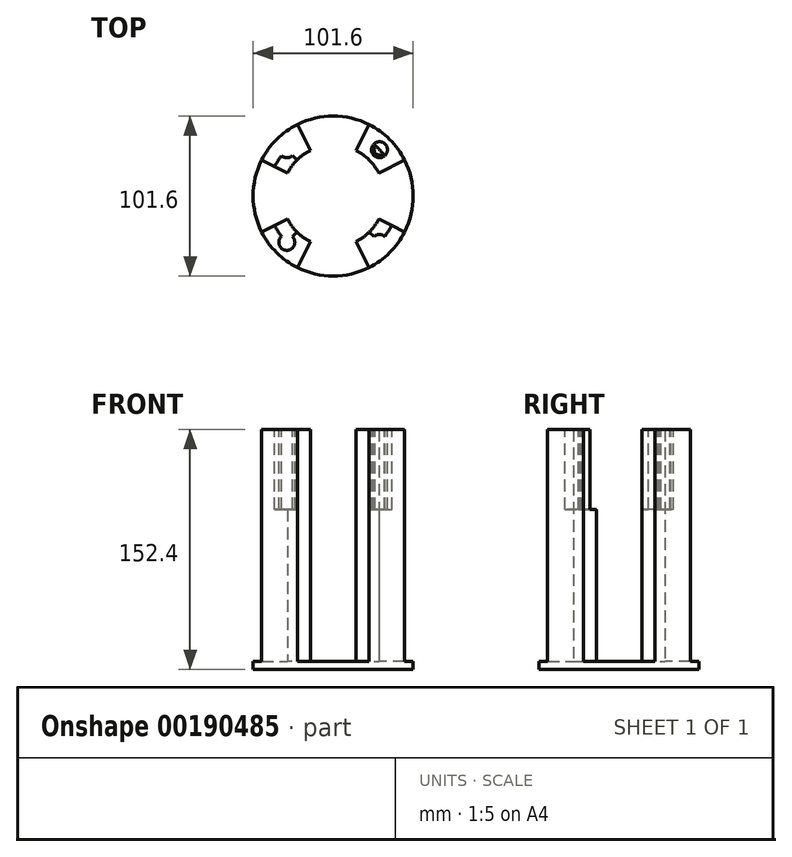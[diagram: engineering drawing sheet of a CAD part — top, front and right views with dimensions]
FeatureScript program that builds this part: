
annotation { "Feature Type Name" : "Feature", "Feature Type Description" : "" }
export const myFeature = defineFeature(function(context is Context, id is Id, definition is map)
    precondition{}
    {
        {
            var Q0;
            Q0=qCreatedBy(makeId("Top.planeOp"),FACE);
            var sketch = newSketch(context, id + "F0", { "sketchPlane" : qUnion([Q0])});
            skLineSegment(sketch, "E0.bottom", {"start": v(0, 0) * mm, "end": v(35.92, 0) * mm});
            skLineSegment(sketch, "E0.top", {"start": v(0, 35.92) * mm, "end": v(35.92, 35.92) * mm});
            skLineSegment(sketch, "E0.left", {"start": v(0, 0) * mm, "end": v(0, 35.92) * mm});
            skLineSegment(sketch, "E0.right", {"start": v(35.92, 0) * mm, "end": v(35.92, 35.92) * mm});
            skCircle(sketch, "E1", {"center": v(0, 0) * mm, "radius": 50.8 * mm});
            skLineSegment(sketch, "E2", {"start": v(0, 0) * mm, "end": v(35.92, 35.92) * mm});
            skPoint(sketch, "E3", {"position": v(17.96, 35.92) * mm});
            skPoint(sketch, "E4", {"position": v(35.92, 17.96) * mm});
            skLineSegment(sketch, "E5", {"start": v(0, 0) * mm, "end": v(17.96, 35.92) * mm});
            skLineSegment(sketch, "E6", {"start": v(0, 0) * mm, "end": v(35.92, 17.96) * mm});
            skLineSegment(sketch, "E7", {"start": v(35.92, 17.96) * mm, "end": v(45.44, 22.72) * mm});
            skLineSegment(sketch, "E8", {"start": v(17.96, 35.92) * mm, "end": v(22.72, 45.44) * mm});
            skCircle(sketch, "E9", {"center": v(0, 0) * mm, "radius": 40.16 * mm});
            skPoint(sketch, "E10.MirrorP", {"position": v(-17.96, 35.92) * mm});
            skPoint(sketch, "E11.MirrorP", {"position": v(-35.92, 17.96) * mm});
            skPoint(sketch, "E12.MirrorP", {"position": v(17.96, -35.92) * mm});
            skPoint(sketch, "E13.MirrorP", {"position": v(35.92, -17.96) * mm});
            skPoint(sketch, "E14.MirrorP", {"position": v(-17.96, -35.92) * mm});
            skPoint(sketch, "E15.MirrorP", {"position": v(-35.92, -17.96) * mm});
            skCircle(sketch, "E16", {"center": v(0, 0) * mm, "radius": 32.43 * mm});
            skLineSegment(sketch, "E17.MirrorCS", {"start": v(0, 0) * mm, "end": v(-17.96, 35.92) * mm});
            skLineSegment(sketch, "E18.MirrorCS", {"start": v(0, 0) * mm, "end": v(-35.92, 17.96) * mm});
            skLineSegment(sketch, "E19.MirrorCS", {"start": v(-35.92, 17.96) * mm, "end": v(-45.44, 22.72) * mm});
            skLineSegment(sketch, "E20.MirrorCS", {"start": v(-17.96, 35.92) * mm, "end": v(-22.72, 45.44) * mm});
            skLineSegment(sketch, "E21.MirrorCS", {"start": v(0, 0) * mm, "end": v(-35.92, -17.96) * mm});
            skLineSegment(sketch, "E22.MirrorCS", {"start": v(0, 0) * mm, "end": v(-17.96, -35.92) * mm});
            skLineSegment(sketch, "E23.MirrorCS", {"start": v(-17.96, -35.92) * mm, "end": v(-22.72, -45.44) * mm});
            skLineSegment(sketch, "E24.MirrorCS", {"start": v(-35.92, -17.96) * mm, "end": v(-45.44, -22.72) * mm});
            skLineSegment(sketch, "E25.MirrorCS", {"start": v(0, 0) * mm, "end": v(17.96, -35.92) * mm});
            skLineSegment(sketch, "E26.MirrorCS", {"start": v(0, 0) * mm, "end": v(35.92, -17.96) * mm});
            skLineSegment(sketch, "E27.MirrorCS", {"start": v(35.92, -17.96) * mm, "end": v(45.44, -22.72) * mm});
            skLineSegment(sketch, "E28.MirrorCS", {"start": v(17.96, -35.92) * mm, "end": v(22.72, -45.44) * mm});
            skSolve(sketch);
        }
        {
            var Q0;
            {var subQ0=sQuery(id+"F0.wireOp",EDGE,"E17.MirrorCS");var subQ1=sQuery(id+"F0.wireOp",EDGE,"E16");var subQ2=makeQuery(id+"F0.imprint","INTERSECT",VERTEX,{"derivedFrom":[subQ1,subQ0]});Q0=makeQuery(id+"F0.imprint","IMPRINT",FACE,{"disambiguationData":[TD([[makeQuery(id+"F0.imprint","IMPRINT",EDGE,{"disambiguationData":[TD([[subQ2,-1.0]])],"derivedFrom":subQ1}),1.0]])]});}
            var Q1;
            {var subQ1=sQuery(id+"F0.wireOp",EDGE,"E0.left");var subQ3=sQuery(id+"F0.wireOp",EDGE,"E16");var subQ4=makeQuery(id+"F0.imprint","INTERSECT",VERTEX,{"derivedFrom":[subQ1,subQ3]});Q1=makeQuery(id+"F0.imprint","IMPRINT",FACE,{"disambiguationData":[TD([[makeQuery(id+"F0.imprint","IMPRINT",EDGE,{"disambiguationData":[TD([[subQ4,-1.0]])],"derivedFrom":subQ3}),1.0]])]});}
            var Q2;
            {var subQ1=sQuery(id+"F0.wireOp",EDGE,"E0.left");var subQ3=sQuery(id+"F0.wireOp",EDGE,"E16");var subQ4=makeQuery(id+"F0.imprint","INTERSECT",VERTEX,{"derivedFrom":[subQ1,subQ3]});Q2=makeQuery(id+"F0.imprint","IMPRINT",FACE,{"disambiguationData":[TD([[makeQuery(id+"F0.imprint","IMPRINT",EDGE,{"disambiguationData":[TD([[subQ4,1.0]])],"derivedFrom":subQ3}),1.0]])]});}
            var Q3;
            {var subQ1=sQuery(id+"F0.wireOp",EDGE,"E2");var subQ3=sQuery(id+"F0.wireOp",EDGE,"E16");var subQ4=makeQuery(id+"F0.imprint","INTERSECT",VERTEX,{"derivedFrom":[subQ1,subQ3]});Q3=makeQuery(id+"F0.imprint","IMPRINT",FACE,{"disambiguationData":[TD([[makeQuery(id+"F0.imprint","IMPRINT",EDGE,{"disambiguationData":[TD([[subQ4,-1.0]])],"derivedFrom":subQ3}),1.0]])]});}
            var Q4;
            {var subQ1=sQuery(id+"F0.wireOp",EDGE,"E2");var subQ3=sQuery(id+"F0.wireOp",EDGE,"E16");var subQ4=makeQuery(id+"F0.imprint","INTERSECT",VERTEX,{"derivedFrom":[subQ1,subQ3]});Q4=makeQuery(id+"F0.imprint","IMPRINT",FACE,{"disambiguationData":[TD([[makeQuery(id+"F0.imprint","IMPRINT",EDGE,{"disambiguationData":[TD([[subQ4,1.0]])],"derivedFrom":subQ3}),1.0]])]});}
            var Q5;
            {var subQ1=sQuery(id+"F0.wireOp",EDGE,"E0.bottom");var subQ3=sQuery(id+"F0.wireOp",EDGE,"E16");var subQ4=makeQuery(id+"F0.imprint","INTERSECT",VERTEX,{"derivedFrom":[subQ1,subQ3]});Q5=makeQuery(id+"F0.imprint","IMPRINT",FACE,{"disambiguationData":[TD([[makeQuery(id+"F0.imprint","IMPRINT",EDGE,{"disambiguationData":[TD([[subQ4,-1.0]])],"derivedFrom":subQ3}),1.0]])]});}
            var Q6;
            {var subQ1=sQuery(id+"F0.wireOp",EDGE,"E0.bottom");var subQ3=sQuery(id+"F0.wireOp",EDGE,"E16");var subQ4=makeQuery(id+"F0.imprint","INTERSECT",VERTEX,{"derivedFrom":[subQ1,subQ3]});Q6=makeQuery(id+"F0.imprint","IMPRINT",FACE,{"disambiguationData":[TD([[makeQuery(id+"F0.imprint","IMPRINT",EDGE,{"disambiguationData":[TD([[subQ4,1.0]])],"derivedFrom":subQ3}),1.0]])]});}
            var Q7;
            {var subQ0=sQuery(id+"F0.wireOp",EDGE,"E25.MirrorCS");var subQ1=sQuery(id+"F0.wireOp",EDGE,"E16");var subQ2=makeQuery(id+"F0.imprint","INTERSECT",VERTEX,{"derivedFrom":[subQ1,subQ0]});Q7=makeQuery(id+"F0.imprint","IMPRINT",FACE,{"disambiguationData":[TD([[makeQuery(id+"F0.imprint","IMPRINT",EDGE,{"disambiguationData":[TD([[subQ2,-1.0]])],"derivedFrom":subQ1}),1.0]])]});}
            var Q8;
            {var subQ0=sQuery(id+"F0.wireOp",EDGE,"E22.MirrorCS");var subQ1=sQuery(id+"F0.wireOp",EDGE,"E16");var subQ2=makeQuery(id+"F0.imprint","INTERSECT",VERTEX,{"derivedFrom":[subQ1,subQ0]});Q8=makeQuery(id+"F0.imprint","IMPRINT",FACE,{"disambiguationData":[TD([[makeQuery(id+"F0.imprint","IMPRINT",EDGE,{"disambiguationData":[TD([[subQ2,-1.0]])],"derivedFrom":subQ1}),1.0]])]});}
            var Q9;
            {var subQ0=sQuery(id+"F0.wireOp",EDGE,"E21.MirrorCS");var subQ1=sQuery(id+"F0.wireOp",EDGE,"E16");var subQ2=makeQuery(id+"F0.imprint","INTERSECT",VERTEX,{"derivedFrom":[subQ1,subQ0]});Q9=makeQuery(id+"F0.imprint","IMPRINT",FACE,{"disambiguationData":[TD([[makeQuery(id+"F0.imprint","IMPRINT",EDGE,{"disambiguationData":[TD([[subQ2,-1.0]])],"derivedFrom":subQ1}),1.0]])]});}
            var Q10;
            {var subQ0=sQuery(id+"F0.wireOp",EDGE,"E18.MirrorCS");var subQ1=sQuery(id+"F0.wireOp",EDGE,"E16");var subQ2=makeQuery(id+"F0.imprint","INTERSECT",VERTEX,{"derivedFrom":[subQ1,subQ0]});Q10=makeQuery(id+"F0.imprint","IMPRINT",FACE,{"disambiguationData":[TD([[makeQuery(id+"F0.imprint","IMPRINT",EDGE,{"disambiguationData":[TD([[subQ2,-1.0]])],"derivedFrom":subQ1}),1.0]])]});}
            var Q11;
            {var subQ0=sQuery(id+"F0.wireOp",EDGE,"E18.MirrorCS");var subQ5=sQuery(id+"F0.wireOp",EDGE,"E16");var subQ6=makeQuery(id+"F0.imprint","INTERSECT",VERTEX,{"derivedFrom":[subQ5,subQ0]});Q11=makeQuery(id+"F0.imprint","IMPRINT",FACE,{"disambiguationData":[TD([[makeQuery(id+"F0.imprint","IMPRINT",EDGE,{"disambiguationData":[TD([[subQ6,-1.0]])],"derivedFrom":subQ5}),-1.0]])]});}
            var Q12;
            {var subQ0=sQuery(id+"F0.wireOp",EDGE,"E17.MirrorCS");var subQ5=sQuery(id+"F0.wireOp",EDGE,"E16");var subQ6=makeQuery(id+"F0.imprint","INTERSECT",VERTEX,{"derivedFrom":[subQ5,subQ0]});Q12=makeQuery(id+"F0.imprint","IMPRINT",FACE,{"disambiguationData":[TD([[makeQuery(id+"F0.imprint","IMPRINT",EDGE,{"disambiguationData":[TD([[subQ6,-1.0]])],"derivedFrom":subQ5}),-1.0]])]});}
            var Q13;
            {var subQ1=sQuery(id+"F0.wireOp",EDGE,"E0.top");var subQ5=sQuery(id+"F0.wireOp",EDGE,"E0.left");var subQ6=makeQuery(id+"F0.imprint","INTERSECT",VERTEX,{"derivedFrom":[subQ1,subQ5]});Q13=makeQuery(id+"F0.imprint","IMPRINT",FACE,{"disambiguationData":[TD([[makeQuery(id+"F0.imprint","IMPRINT",EDGE,{"disambiguationData":[TD([[subQ6,1.0]])],"derivedFrom":subQ5}),1.0]])]});}
            var Q14;
            {var subQ0=sQuery(id+"F0.wireOp",EDGE,"E0.left");var subQ1=sQuery(id+"F0.wireOp",EDGE,"E0.top");var subQ2=makeQuery(id+"F0.imprint","INTERSECT",VERTEX,{"derivedFrom":[subQ1,subQ0]});Q14=makeQuery(id+"F0.imprint","IMPRINT",FACE,{"disambiguationData":[TD([[makeQuery(id+"F0.imprint","IMPRINT",EDGE,{"disambiguationData":[TD([[subQ2,1.0]])],"derivedFrom":subQ0}),-1.0]])]});}
            var Q15;
            {var subQ0=sQuery(id+"F0.wireOp",EDGE,"E16");var subQ1=sQuery(id+"F0.wireOp",EDGE,"E2");var subQ2=makeQuery(id+"F0.imprint","INTERSECT",VERTEX,{"derivedFrom":[subQ1,subQ0]});Q15=makeQuery(id+"F0.imprint","IMPRINT",FACE,{"disambiguationData":[TD([[makeQuery(id+"F0.imprint","IMPRINT",EDGE,{"disambiguationData":[TD([[subQ2,-1.0]])],"derivedFrom":subQ1}),1.0]])]});}
            var Q16;
            {var subQ0=sQuery(id+"F0.wireOp",EDGE,"E2");var subQ3=sQuery(id+"F0.wireOp",EDGE,"E9");var subQ5=makeQuery(id+"F0.imprint","INTERSECT",VERTEX,{"derivedFrom":[subQ0,subQ3]});Q16=makeQuery(id+"F0.imprint","IMPRINT",FACE,{"disambiguationData":[TD([[makeQuery(id+"F0.imprint","IMPRINT",EDGE,{"disambiguationData":[TD([[subQ5,-1.0]])],"derivedFrom":subQ0}),1.0]])]});}
            var Q17;
            {var subQ0=sQuery(id+"F0.wireOp",EDGE,"E2");var subQ3=sQuery(id+"F0.wireOp",EDGE,"E9");var subQ5=makeQuery(id+"F0.imprint","INTERSECT",VERTEX,{"derivedFrom":[subQ0,subQ3]});Q17=makeQuery(id+"F0.imprint","IMPRINT",FACE,{"disambiguationData":[TD([[makeQuery(id+"F0.imprint","IMPRINT",EDGE,{"disambiguationData":[TD([[subQ5,-1.0]])],"derivedFrom":subQ0}),-1.0]])]});}
            var Q18;
            {var subQ0=sQuery(id+"F0.wireOp",EDGE,"E16");var subQ1=sQuery(id+"F0.wireOp",EDGE,"E2");var subQ2=makeQuery(id+"F0.imprint","INTERSECT",VERTEX,{"derivedFrom":[subQ1,subQ0]});Q18=makeQuery(id+"F0.imprint","IMPRINT",FACE,{"disambiguationData":[TD([[makeQuery(id+"F0.imprint","IMPRINT",EDGE,{"disambiguationData":[TD([[subQ2,-1.0]])],"derivedFrom":subQ1}),-1.0]])]});}
            var Q19;
            {var subQ0=sQuery(id+"F0.wireOp",EDGE,"E0.right");var subQ1=sQuery(id+"F0.wireOp",EDGE,"E0.bottom");var subQ2=makeQuery(id+"F0.imprint","INTERSECT",VERTEX,{"derivedFrom":[subQ1,subQ0]});Q19=makeQuery(id+"F0.imprint","IMPRINT",FACE,{"disambiguationData":[TD([[makeQuery(id+"F0.imprint","IMPRINT",EDGE,{"disambiguationData":[TD([[subQ2,1.0]])],"derivedFrom":subQ1}),1.0]])]});}
            var Q20;
            {var subQ1=sQuery(id+"F0.wireOp",EDGE,"E0.bottom");var subQ6=sQuery(id+"F0.wireOp",EDGE,"E0.right");var subQ9=makeQuery(id+"F0.imprint","INTERSECT",VERTEX,{"derivedFrom":[subQ1,subQ6]});Q20=makeQuery(id+"F0.imprint","IMPRINT",FACE,{"disambiguationData":[TD([[makeQuery(id+"F0.imprint","IMPRINT",EDGE,{"disambiguationData":[TD([[subQ9,1.0]])],"derivedFrom":subQ1}),-1.0]])]});}
            var Q21;
            {var subQ0=sQuery(id+"F0.wireOp",EDGE,"E25.MirrorCS");var subQ5=sQuery(id+"F0.wireOp",EDGE,"E16");var subQ6=makeQuery(id+"F0.imprint","INTERSECT",VERTEX,{"derivedFrom":[subQ5,subQ0]});Q21=makeQuery(id+"F0.imprint","IMPRINT",FACE,{"disambiguationData":[TD([[makeQuery(id+"F0.imprint","IMPRINT",EDGE,{"disambiguationData":[TD([[subQ6,-1.0]])],"derivedFrom":subQ5}),-1.0]])]});}
            var Q22;
            {var subQ0=sQuery(id+"F0.wireOp",EDGE,"E22.MirrorCS");var subQ5=sQuery(id+"F0.wireOp",EDGE,"E16");var subQ6=makeQuery(id+"F0.imprint","INTERSECT",VERTEX,{"derivedFrom":[subQ5,subQ0]});Q22=makeQuery(id+"F0.imprint","IMPRINT",FACE,{"disambiguationData":[TD([[makeQuery(id+"F0.imprint","IMPRINT",EDGE,{"disambiguationData":[TD([[subQ6,-1.0]])],"derivedFrom":subQ5}),-1.0]])]});}
            var Q23;
            {var subQ0=sQuery(id+"F0.wireOp",EDGE,"E21.MirrorCS");var subQ5=sQuery(id+"F0.wireOp",EDGE,"E16");var subQ6=makeQuery(id+"F0.imprint","INTERSECT",VERTEX,{"derivedFrom":[subQ5,subQ0]});Q23=makeQuery(id+"F0.imprint","IMPRINT",FACE,{"disambiguationData":[TD([[makeQuery(id+"F0.imprint","IMPRINT",EDGE,{"disambiguationData":[TD([[subQ6,-1.0]])],"derivedFrom":subQ5}),-1.0]])]});}
            var Q24;
            {var subQ0=sQuery(id+"F0.wireOp",EDGE,"E23.MirrorCS");Q24=makeQuery(id+"F0.imprint","IMPRINT",FACE,{"disambiguationData":[TD([[makeQuery(id+"F0.imprint","IMPRINT",EDGE,{"derivedFrom":subQ0}),-1.0]])]});}
            var Q25;
            {var subQ0=sQuery(id+"F0.wireOp",EDGE,"E19.MirrorCS");Q25=makeQuery(id+"F0.imprint","IMPRINT",FACE,{"disambiguationData":[TD([[makeQuery(id+"F0.imprint","IMPRINT",EDGE,{"derivedFrom":subQ0}),1.0]])]});}
            var Q26;
            {var subQ0=sQuery(id+"F0.wireOp",EDGE,"E19.MirrorCS");Q26=makeQuery(id+"F0.imprint","IMPRINT",FACE,{"disambiguationData":[TD([[makeQuery(id+"F0.imprint","IMPRINT",EDGE,{"derivedFrom":subQ0}),-1.0]])]});}
            var Q27;
            {var subQ0=sQuery(id+"F0.wireOp",EDGE,"E8");Q27=makeQuery(id+"F0.imprint","IMPRINT",FACE,{"disambiguationData":[TD([[makeQuery(id+"F0.imprint","IMPRINT",EDGE,{"derivedFrom":subQ0}),1.0]])]});}
            var Q28;
            {var subQ3=sQuery(id+"F0.wireOp",EDGE,"E8");Q28=makeQuery(id+"F0.imprint","IMPRINT",FACE,{"disambiguationData":[TD([[makeQuery(id+"F0.imprint","IMPRINT",EDGE,{"derivedFrom":subQ3}),-1.0]])]});}
            var Q29;
            {var subQ3=sQuery(id+"F0.wireOp",EDGE,"E7");Q29=makeQuery(id+"F0.imprint","IMPRINT",FACE,{"disambiguationData":[TD([[makeQuery(id+"F0.imprint","IMPRINT",EDGE,{"derivedFrom":subQ3}),1.0]])]});}
            var Q30;
            {var subQ0=sQuery(id+"F0.wireOp",EDGE,"E7");Q30=makeQuery(id+"F0.imprint","IMPRINT",FACE,{"disambiguationData":[TD([[makeQuery(id+"F0.imprint","IMPRINT",EDGE,{"derivedFrom":subQ0}),-1.0]])]});}
            var Q31;
            {var subQ0=sQuery(id+"F0.wireOp",EDGE,"E27.MirrorCS");Q31=makeQuery(id+"F0.imprint","IMPRINT",FACE,{"disambiguationData":[TD([[makeQuery(id+"F0.imprint","IMPRINT",EDGE,{"derivedFrom":subQ0}),-1.0]])]});}
            var Q32;
            {var subQ0=sQuery(id+"F0.wireOp",EDGE,"E23.MirrorCS");Q32=makeQuery(id+"F0.imprint","IMPRINT",FACE,{"disambiguationData":[TD([[makeQuery(id+"F0.imprint","IMPRINT",EDGE,{"derivedFrom":subQ0}),1.0]])]});}
            extrude(context, id + "F1", {"entities" : qUnion([Q0, Q1, Q2, Q3, Q4, Q5, Q6, Q7, Q8, Q9, Q10, Q11, Q12, Q13, Q14, Q15, Q16, Q17, Q18, Q19, Q20, Q21, Q22, Q23, Q24, Q25, Q26, Q27, Q28, Q29, Q30, Q31, Q32]), "depth" : 5.08 * mm});
        }
        {
            var Q0;
            {var subQ0=sQuery(id+"F0.wireOp",EDGE,"E21.MirrorCS");var subQ5=sQuery(id+"F0.wireOp",EDGE,"E16");var subQ6=makeQuery(id+"F0.imprint","INTERSECT",VERTEX,{"derivedFrom":[subQ5,subQ0]});Q0=makeQuery(id+"F0.imprint","IMPRINT",FACE,{"disambiguationData":[TD([[makeQuery(id+"F0.imprint","IMPRINT",EDGE,{"disambiguationData":[TD([[subQ6,-1.0]])],"derivedFrom":subQ5}),-1.0]])]});}
            var Q1;
            {var subQ0=sQuery(id+"F0.wireOp",EDGE,"E23.MirrorCS");Q1=makeQuery(id+"F0.imprint","IMPRINT",FACE,{"disambiguationData":[TD([[makeQuery(id+"F0.imprint","IMPRINT",EDGE,{"derivedFrom":subQ0}),-1.0]])]});}
            var Q2;
            {var subQ0=sQuery(id+"F0.wireOp",EDGE,"E17.MirrorCS");var subQ5=sQuery(id+"F0.wireOp",EDGE,"E16");var subQ6=makeQuery(id+"F0.imprint","INTERSECT",VERTEX,{"derivedFrom":[subQ5,subQ0]});Q2=makeQuery(id+"F0.imprint","IMPRINT",FACE,{"disambiguationData":[TD([[makeQuery(id+"F0.imprint","IMPRINT",EDGE,{"disambiguationData":[TD([[subQ6,-1.0]])],"derivedFrom":subQ5}),-1.0]])]});}
            var Q3;
            {var subQ0=sQuery(id+"F0.wireOp",EDGE,"E19.MirrorCS");Q3=makeQuery(id+"F0.imprint","IMPRINT",FACE,{"disambiguationData":[TD([[makeQuery(id+"F0.imprint","IMPRINT",EDGE,{"derivedFrom":subQ0}),-1.0]])]});}
            var Q4;
            {var subQ3=sQuery(id+"F0.wireOp",EDGE,"E8");Q4=makeQuery(id+"F0.imprint","IMPRINT",FACE,{"disambiguationData":[TD([[makeQuery(id+"F0.imprint","IMPRINT",EDGE,{"derivedFrom":subQ3}),-1.0]])]});}
            var Q5;
            {var subQ0=sQuery(id+"F0.wireOp",EDGE,"E2");var subQ3=sQuery(id+"F0.wireOp",EDGE,"E9");var subQ5=makeQuery(id+"F0.imprint","INTERSECT",VERTEX,{"derivedFrom":[subQ0,subQ3]});Q5=makeQuery(id+"F0.imprint","IMPRINT",FACE,{"disambiguationData":[TD([[makeQuery(id+"F0.imprint","IMPRINT",EDGE,{"disambiguationData":[TD([[subQ5,-1.0]])],"derivedFrom":subQ0}),1.0]])]});}
            var Q6;
            {var subQ0=sQuery(id+"F0.wireOp",EDGE,"E2");var subQ3=sQuery(id+"F0.wireOp",EDGE,"E9");var subQ5=makeQuery(id+"F0.imprint","INTERSECT",VERTEX,{"derivedFrom":[subQ0,subQ3]});Q6=makeQuery(id+"F0.imprint","IMPRINT",FACE,{"disambiguationData":[TD([[makeQuery(id+"F0.imprint","IMPRINT",EDGE,{"disambiguationData":[TD([[subQ5,-1.0]])],"derivedFrom":subQ0}),-1.0]])]});}
            var Q7;
            {var subQ3=sQuery(id+"F0.wireOp",EDGE,"E7");Q7=makeQuery(id+"F0.imprint","IMPRINT",FACE,{"disambiguationData":[TD([[makeQuery(id+"F0.imprint","IMPRINT",EDGE,{"derivedFrom":subQ3}),1.0]])]});}
            var Q8;
            {var subQ0=sQuery(id+"F0.wireOp",EDGE,"E27.MirrorCS");Q8=makeQuery(id+"F0.imprint","IMPRINT",FACE,{"disambiguationData":[TD([[makeQuery(id+"F0.imprint","IMPRINT",EDGE,{"derivedFrom":subQ0}),-1.0]])]});}
            var Q9;
            {var subQ0=sQuery(id+"F0.wireOp",EDGE,"E16");var subQ1=sQuery(id+"F0.wireOp",EDGE,"E2");var subQ2=makeQuery(id+"F0.imprint","INTERSECT",VERTEX,{"derivedFrom":[subQ1,subQ0]});Q9=makeQuery(id+"F0.imprint","IMPRINT",FACE,{"disambiguationData":[TD([[makeQuery(id+"F0.imprint","IMPRINT",EDGE,{"disambiguationData":[TD([[subQ2,-1.0]])],"derivedFrom":subQ1}),1.0]])]});}
            var Q10;
            {var subQ0=sQuery(id+"F0.wireOp",EDGE,"E16");var subQ1=sQuery(id+"F0.wireOp",EDGE,"E2");var subQ2=makeQuery(id+"F0.imprint","INTERSECT",VERTEX,{"derivedFrom":[subQ1,subQ0]});Q10=makeQuery(id+"F0.imprint","IMPRINT",FACE,{"disambiguationData":[TD([[makeQuery(id+"F0.imprint","IMPRINT",EDGE,{"disambiguationData":[TD([[subQ2,-1.0]])],"derivedFrom":subQ1}),-1.0]])]});}
            var Q11;
            {var subQ0=sQuery(id+"F0.wireOp",EDGE,"E25.MirrorCS");var subQ5=sQuery(id+"F0.wireOp",EDGE,"E16");var subQ6=makeQuery(id+"F0.imprint","INTERSECT",VERTEX,{"derivedFrom":[subQ5,subQ0]});Q11=makeQuery(id+"F0.imprint","IMPRINT",FACE,{"disambiguationData":[TD([[makeQuery(id+"F0.imprint","IMPRINT",EDGE,{"disambiguationData":[TD([[subQ6,-1.0]])],"derivedFrom":subQ5}),-1.0]])]});}
            extrude(context, id + "F2", {"entities" : qUnion([Q0, Q1, Q2, Q3, Q4, Q5, Q6, Q7, Q8, Q9, Q10, Q11]), "operationType" : NewBodyOperationType.ADD, "depth" : 152.4 * mm});
        }
        {
            var Q0;
            Q0=makeQuery(id+"F2.opExtrude","CAP_FACE",FACE,{"disambiguationData":[OSD([sQuery(id+"F0.wireOp",EDGE,"E1"),sQuery(id+"F0.wireOp",EDGE,"E5"),sQuery(id+"F0.wireOp",EDGE,"E6"),sQuery(id+"F0.wireOp",EDGE,"E7"),sQuery(id+"F0.wireOp",EDGE,"E8"),sQuery(id+"F0.wireOp",EDGE,"E16")])],"isStart":false});
            var sketch = newSketch(context, id + "F3", { "sketchPlane" : qUnion([Q0])});
            skLineSegment(sketch, "E29", {"start": v(22.72, 45.44) * mm, "end": v(29, 14.5) * mm});
            skLineSegment(sketch, "E30", {"start": v(14.5, 29) * mm, "end": v(45.44, 22.72) * mm});
            skLineSegment(sketch, "E31", {"start": v(35.92, 35.92) * mm, "end": v(22.93, 22.93) * mm});
            skPoint(sketch, "E32", {"position": v(29.43, 29.43) * mm});
            skCircle(sketch, "E33", {"center": v(29.43, 29.43) * mm, "radius": 5.08 * mm});
            skLineSegment(sketch, "E34", {"start": v(29.43, 29.43) * mm, "end": v(34.5, 29.43) * mm});
            skCircle(sketch, "E35.MirrorC", {"center": v(29.43, -29.43) * mm, "radius": 5.08 * mm});
            skCircle(sketch, "E36.MirrorC", {"center": v(-29.43, 29.43) * mm, "radius": 5.08 * mm});
            skCircle(sketch, "E37.MirrorC", {"center": v(-29.43, -29.43) * mm, "radius": 5.08 * mm});
            skLineSegment(sketch, "E38", {"start": v(-29.43, -29.43) * mm, "end": v(29.43, 29.43) * mm});
            skLineSegment(sketch, "E39", {"start": v(29.43, -29.43) * mm, "end": v(-29.43, 29.43) * mm});
            skArc(sketch, "E40", {"start": v(29.43, -29.43) * mm, "mid": v(0, 41.62) * mm, "end": v(-29.43, -29.43) * mm});
            skCircle(sketch, "E41", {"center": v(0, 0) * mm, "radius": 50.8 * mm});
            skSolve(sketch);
        }
        {
            var Q0;
            Q0=makeQuery(id+"F3.imprint","IMPRINT",FACE,{"disambiguationData":[TD([[makeQuery(id+"F3.imprint","IMPRINT",EDGE,{"derivedFrom":sQuery(id+"F3.wireOp",EDGE,"E36.MirrorC")}),-1.0]])]});
            var Q1;
            Q1=makeQuery(id+"F3.imprint","IMPRINT",FACE,{"disambiguationData":[TD([[makeQuery(id+"F3.imprint","IMPRINT",EDGE,{"derivedFrom":sQuery(id+"F3.wireOp",EDGE,"E35.MirrorC")}),-1.0]])]});
            var Q2;
            Q2=makeQuery(id+"F3.imprint","IMPRINT",FACE,{"disambiguationData":[TD([[makeQuery(id+"F3.imprint","IMPRINT",EDGE,{"derivedFrom":sQuery(id+"F3.wireOp",EDGE,"E37.MirrorC")}),1.0]])]});
            var Q3;
            {var subQ3=sQuery(id+"F3.wireOp",EDGE,"E31");var subQ5=makeQuery(id+"F3.imprint","INTERSECT",VERTEX,{"derivedFrom":[subQ3,sQuery(id+"F3.wireOp",EDGE,"E34")]});Q3=makeQuery(id+"F3.imprint","IMPRINT",FACE,{"disambiguationData":[TD([[makeQuery(id+"F3.imprint","IMPRINT",EDGE,{"disambiguationData":[TD([[subQ5,1.0]])],"derivedFrom":subQ3}),-1.0]])]});}
            var Q4;
            {var subQ0=sQuery(id+"F3.wireOp",EDGE,"E33");var subQ1=sQuery(id+"F3.wireOp",EDGE,"E29");var subQ2=makeQuery(id+"F3.imprint","INTERSECT",VERTEX,{"disambiguationData":[OD(0.0)],"derivedFrom":[subQ1,subQ0]});Q4=makeQuery(id+"F3.imprint","IMPRINT",FACE,{"disambiguationData":[TD([[makeQuery(id+"F3.imprint","IMPRINT",EDGE,{"disambiguationData":[TD([[subQ2,-1.0]])],"derivedFrom":subQ0}),1.0]])]});}
            var Q5;
            {var subQ0=sQuery(id+"F3.wireOp",EDGE,"E33");var subQ1=sQuery(id+"F3.wireOp",EDGE,"E30");var subQ2=makeQuery(id+"F3.imprint","INTERSECT",VERTEX,{"disambiguationData":[OD(0.0)],"derivedFrom":[subQ1,subQ0]});Q5=makeQuery(id+"F3.imprint","IMPRINT",FACE,{"disambiguationData":[TD([[makeQuery(id+"F3.imprint","IMPRINT",EDGE,{"disambiguationData":[TD([[subQ2,-1.0]])],"derivedFrom":subQ0}),1.0]])]});}
            var Q6;
            {var subQ0=sQuery(id+"F3.wireOp",EDGE,"E33");var subQ1=sQuery(id+"F3.wireOp",EDGE,"E29");var subQ2=makeQuery(id+"F3.imprint","INTERSECT",VERTEX,{"disambiguationData":[OD(1.0)],"derivedFrom":[subQ1,subQ0]});Q6=makeQuery(id+"F3.imprint","IMPRINT",FACE,{"disambiguationData":[TD([[makeQuery(id+"F3.imprint","IMPRINT",EDGE,{"disambiguationData":[TD([[subQ2,1.0]])],"derivedFrom":subQ0}),1.0]])]});}
            var Q7;
            {var subQ0=sQuery(id+"F3.wireOp",EDGE,"E33");var subQ1=sQuery(id+"F3.wireOp",EDGE,"E29");var subQ2=makeQuery(id+"F3.imprint","INTERSECT",VERTEX,{"disambiguationData":[OD(1.0)],"derivedFrom":[subQ1,subQ0]});Q7=makeQuery(id+"F3.imprint","IMPRINT",FACE,{"disambiguationData":[TD([[makeQuery(id+"F3.imprint","IMPRINT",EDGE,{"disambiguationData":[TD([[subQ2,-1.0]])],"derivedFrom":subQ0}),1.0]])]});}
            var Q8;
            {var subQ5=sQuery(id+"F3.wireOp",EDGE,"E34");Q8=makeQuery(id+"F3.imprint","IMPRINT",FACE,{"disambiguationData":[TD([[makeQuery(id+"F3.imprint","IMPRINT",EDGE,{"derivedFrom":subQ5}),-1.0]])]});}
            var Q9;
            {var subQ0=sQuery(id+"F3.wireOp",EDGE,"E34");Q9=makeQuery(id+"F3.imprint","IMPRINT",FACE,{"disambiguationData":[TD([[makeQuery(id+"F3.imprint","IMPRINT",EDGE,{"derivedFrom":subQ0}),1.0]])]});}
            extrude(context, id + "F4", {"entities" : qUnion([Q0, Q1, Q2, Q3, Q4, Q5, Q6, Q7, Q8, Q9]), "operationType" : NewBodyOperationType.REMOVE, "oppositeDirection" : true, "depth" : 50.8 * mm});
        }
    });
